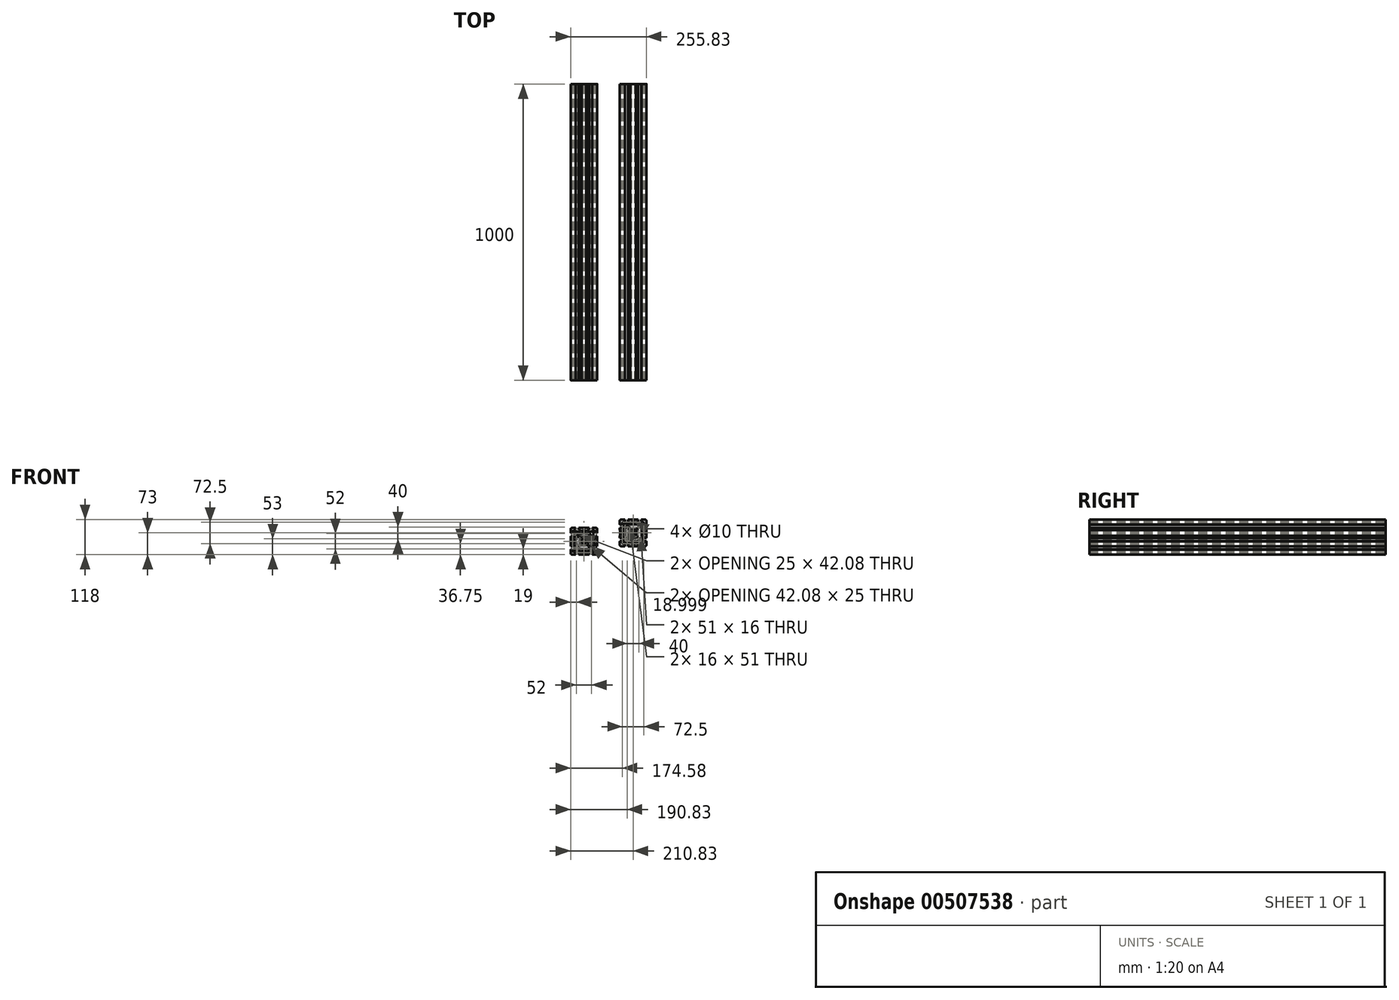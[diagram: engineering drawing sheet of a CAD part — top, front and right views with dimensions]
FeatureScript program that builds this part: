
annotation { "Feature Type Name" : "Feature", "Feature Type Description" : "" }
export const myFeature = defineFeature(function(context is Context, id is Id, definition is map)
    precondition{}
    {
        {
            var Q0;
            Q0=qCreatedBy(makeId("Front.planeOp"),FACE);
            var sketch = newSketch(context, id + "F0", { "sketchPlane" : qUnion([Q0])});
            skLineSegment(sketch, "E0", {"start": v(28, 45) * mm, "end": v(28, 44.5) * mm});
            skLineSegment(sketch, "E1", {"start": v(28, 44.5) * mm, "end": v(27.5, 44.5) * mm});
            skLineSegment(sketch, "E2", {"start": v(27.5, 44.5) * mm, "end": v(27.5, 39) * mm});
            skLineSegment(sketch, "E3", {"start": v(27.5, 39) * mm, "end": v(33.5, 39) * mm});
            skLineSegment(sketch, "E4", {"start": v(33.5, 39) * mm, "end": v(33.5, 36) * mm});
            skLineSegment(sketch, "E5", {"start": v(33.5, 36) * mm, "end": v(29.5, 32) * mm});
            skLineSegment(sketch, "E6", {"start": v(29.5, 32) * mm, "end": v(12.5, 32) * mm});
            skLineSegment(sketch, "E7", {"start": v(12.5, 32) * mm, "end": v(12.5, 39) * mm});
            skLineSegment(sketch, "E8", {"start": v(12.5, 39) * mm, "end": v(17.5, 39) * mm});
            skLineSegment(sketch, "E9", {"start": v(17.5, 39) * mm, "end": v(17.5, 44.5) * mm});
            skLineSegment(sketch, "E10", {"start": v(17.5, 44.5) * mm, "end": v(17, 44.5) * mm});
            skLineSegment(sketch, "E11", {"start": v(17, 44.5) * mm, "end": v(17, 45) * mm});
            skLineSegment(sketch, "E12", {"start": v(45, 28) * mm, "end": v(44.5, 28) * mm});
            skLineSegment(sketch, "E13", {"start": v(44.5, 28) * mm, "end": v(44.5, 27.5) * mm});
            skLineSegment(sketch, "E14", {"start": v(44.5, 27.5) * mm, "end": v(39, 27.5) * mm});
            skLineSegment(sketch, "E15", {"start": v(39, 27.5) * mm, "end": v(39, 33.5) * mm});
            skLineSegment(sketch, "E16", {"start": v(39, 33.5) * mm, "end": v(36, 33.5) * mm});
            skLineSegment(sketch, "E17", {"start": v(36, 33.5) * mm, "end": v(32, 29.5) * mm});
            skLineSegment(sketch, "E18", {"start": v(32, 29.5) * mm, "end": v(32, 12.5) * mm});
            skLineSegment(sketch, "E19", {"start": v(32, 12.5) * mm, "end": v(39, 12.5) * mm});
            skLineSegment(sketch, "E20", {"start": v(39, 12.5) * mm, "end": v(39, 17.5) * mm});
            skLineSegment(sketch, "E21", {"start": v(39, 17.5) * mm, "end": v(44.5, 17.5) * mm});
            skLineSegment(sketch, "E22", {"start": v(44.5, 17.5) * mm, "end": v(44.5, 17) * mm});
            skLineSegment(sketch, "E23", {"start": v(44.5, 17) * mm, "end": v(45, 17) * mm});
            skLineSegment(sketch, "E24", {"start": v(45, 28) * mm, "end": v(45, 40) * mm});
            skLineSegment(sketch, "E25", {"start": v(28, 45) * mm, "end": v(40, 45) * mm});
            skPoint(sketch, "E26.visualSharp", {"position": v(45, 45) * mm});
            skArc(sketch, "E26.filletArc", {"start": v(45, 40) * mm, "mid": v(43.54, 43.54) * mm, "end": v(40, 45) * mm});
            skLineSegment(sketch, "E27", {"start": v(17, 45) * mm, "end": v(9.5, 45) * mm});
            skLineSegment(sketch, "E28", {"start": v(9.5, 45) * mm, "end": v(9.5, 44.5) * mm});
            skLineSegment(sketch, "E29", {"start": v(9.5, 44.5) * mm, "end": v(0, 44.5) * mm});
            skLineSegment(sketch, "E30", {"start": v(0, 44.5) * mm, "end": v(0, 41.25) * mm});
            skLineSegment(sketch, "E31", {"start": v(45, 17) * mm, "end": v(45, 9.5) * mm});
            skLineSegment(sketch, "E32", {"start": v(45, 9.5) * mm, "end": v(44.5, 9.5) * mm});
            skLineSegment(sketch, "E33", {"start": v(44.5, 9.5) * mm, "end": v(44.5, 0) * mm});
            skLineSegment(sketch, "E34", {"start": v(44.5, 0) * mm, "end": v(41.25, 0) * mm});
            skLineSegment(sketch, "E35.bottom", {"start": v(7.5, 0) * mm, "end": v(12, 0) * mm});
            skLineSegment(sketch, "E35.top", {"start": v(0, 28) * mm, "end": v(25.5, 28) * mm});
            skLineSegment(sketch, "E35.right", {"start": v(28, 0) * mm, "end": v(28, 25.5) * mm});
            skLineSegment(sketch, "E36.top", {"start": v(0, 12) * mm, "end": v(9.5, 12) * mm});
            skLineSegment(sketch, "E36.left", {"start": v(0, 7.5) * mm, "end": v(0, 12) * mm});
            skLineSegment(sketch, "E36.right", {"start": v(12, 0) * mm, "end": v(12, 9.5) * mm});
            skArc(sketch, "E37", {"start": v(7.5, 0) * mm, "mid": v(5.3, 5.3) * mm, "end": v(0, 7.5) * mm});
            skLineSegment(sketch, "E38", {"start": v(25.5, 28) * mm, "end": v(9.5, 12) * mm});
            skLineSegment(sketch, "E39", {"start": v(28, 25.5) * mm, "end": v(12, 9.5) * mm});
            skLineSegment(sketch, "E40.trimOffspring", {"start": v(12, 0) * mm, "end": v(7.5, 0) * mm});
            skLineSegment(sketch, "E41.trimOffspring", {"start": v(0, 12) * mm, "end": v(0, 7.5) * mm});
            skArc(sketch, "E42", {"start": v(41.25, 0) * mm, "mid": v(36.25, 5) * mm, "end": v(31.25, 0) * mm});
            skArc(sketch, "E43", {"start": v(0, 31.25) * mm, "mid": v(5, 36.25) * mm, "end": v(0, 41.25) * mm});
            skLineSegment(sketch, "E44.trimOffspring", {"start": v(0, 31.25) * mm, "end": v(0, 28) * mm});
            skLineSegment(sketch, "E45.trimOffspring", {"start": v(31.25, 0) * mm, "end": v(28, 0) * mm});
            skLineSegment(sketch, "E46.1.0", {"start": v(-28, 0) * mm, "end": v(-28, 25.5) * mm});
            skLineSegment(sketch, "E46.1.1", {"start": v(0, 28) * mm, "end": v(-25.5, 28) * mm});
            skPoint(sketch, "E46.1.2", {"position": v(-45, 45) * mm});
            skArc(sketch, "E46.1.3", {"start": v(0, 41.25) * mm, "mid": v(-5, 36.25) * mm, "end": v(0, 31.25) * mm});
            skLineSegment(sketch, "E46.1.4", {"start": v(-25.5, 28) * mm, "end": v(-9.5, 12) * mm});
            skLineSegment(sketch, "E46.1.5", {"start": v(-44.5, 9.5) * mm, "end": v(-44.5, 0) * mm});
            skLineSegment(sketch, "E46.1.6", {"start": v(-28, 25.5) * mm, "end": v(-12, 9.5) * mm});
            skLineSegment(sketch, "E46.1.7", {"start": v(-28, 45) * mm, "end": v(-40, 45) * mm});
            skLineSegment(sketch, "E46.1.8", {"start": v(-32, 29.5) * mm, "end": v(-32, 12.5) * mm});
            skArc(sketch, "E46.1.9", {"start": v(-31.25, 0) * mm, "mid": v(-36.25, 5) * mm, "end": v(-41.25, 0) * mm});
            skLineSegment(sketch, "E46.1.10", {"start": v(-9.5, 44.5) * mm, "end": v(0, 44.5) * mm});
            skLineSegment(sketch, "E46.1.11", {"start": v(-12.5, 32) * mm, "end": v(-12.5, 39) * mm});
            skLineSegment(sketch, "E46.1.12", {"start": v(-12, 0) * mm, "end": v(-12, 9.5) * mm});
            skLineSegment(sketch, "E46.1.13", {"start": v(-45, 17) * mm, "end": v(-45, 9.5) * mm});
            skArc(sketch, "E46.1.14", {"start": v(-40, 45) * mm, "mid": v(-43.54, 43.54) * mm, "end": v(-45, 40) * mm});
            skArc(sketch, "E46.1.15", {"start": v(0, 7.5) * mm, "mid": v(-5.3, 5.3) * mm, "end": v(-7.5, 0) * mm});
            skLineSegment(sketch, "E46.1.16", {"start": v(-45, 28) * mm, "end": v(-45, 40) * mm});
            skLineSegment(sketch, "E46.1.17", {"start": v(0, 12) * mm, "end": v(-9.5, 12) * mm});
            skLineSegment(sketch, "E46.1.18", {"start": v(-17, 45) * mm, "end": v(-9.5, 45) * mm});
            skLineSegment(sketch, "E46.1.19", {"start": v(-32, 12.5) * mm, "end": v(-39, 12.5) * mm});
            skLineSegment(sketch, "E46.1.20", {"start": v(-29.5, 32) * mm, "end": v(-12.5, 32) * mm});
            skLineSegment(sketch, "E46.1.21", {"start": v(-12.5, 39) * mm, "end": v(-17.5, 39) * mm});
            skLineSegment(sketch, "E46.1.22", {"start": v(-17.5, 39) * mm, "end": v(-17.5, 44.5) * mm});
            skLineSegment(sketch, "E46.1.23", {"start": v(-44.5, 0) * mm, "end": v(-41.25, 0) * mm});
            skLineSegment(sketch, "E46.1.24", {"start": v(-27.5, 39) * mm, "end": v(-33.5, 39) * mm});
            skLineSegment(sketch, "E46.1.25", {"start": v(-36, 33.5) * mm, "end": v(-32, 29.5) * mm});
            skLineSegment(sketch, "E46.1.26", {"start": v(-39, 12.5) * mm, "end": v(-39, 17.5) * mm});
            skLineSegment(sketch, "E46.1.27", {"start": v(-39, 17.5) * mm, "end": v(-44.5, 17.5) * mm});
            skLineSegment(sketch, "E46.1.28", {"start": v(-33.5, 39) * mm, "end": v(-33.5, 36) * mm});
            skLineSegment(sketch, "E46.1.29", {"start": v(-33.5, 36) * mm, "end": v(-29.5, 32) * mm});
            skLineSegment(sketch, "E46.1.30", {"start": v(-31.25, 0) * mm, "end": v(-28, 0) * mm});
            skLineSegment(sketch, "E46.1.33", {"start": v(-12, 0) * mm, "end": v(-7.5, 0) * mm});
            skLineSegment(sketch, "E46.1.34", {"start": v(-27.5, 44.5) * mm, "end": v(-27.5, 39) * mm});
            skLineSegment(sketch, "E46.1.35", {"start": v(-44.5, 27.5) * mm, "end": v(-39, 27.5) * mm});
            skLineSegment(sketch, "E46.1.36", {"start": v(-39, 27.5) * mm, "end": v(-39, 33.5) * mm});
            skLineSegment(sketch, "E46.1.37", {"start": v(-39, 33.5) * mm, "end": v(-36, 33.5) * mm});
            skLineSegment(sketch, "E46.1.39", {"start": v(-7.5, 0) * mm, "end": v(-12, 0) * mm});
            skLineSegment(sketch, "E46.1.40", {"start": v(-45, 28) * mm, "end": v(-44.5, 28) * mm});
            skLineSegment(sketch, "E46.1.41", {"start": v(-44.5, 28) * mm, "end": v(-44.5, 27.5) * mm});
            skLineSegment(sketch, "E46.1.42", {"start": v(-9.5, 45) * mm, "end": v(-9.5, 44.5) * mm});
            skLineSegment(sketch, "E46.1.43", {"start": v(-17.5, 44.5) * mm, "end": v(-17, 44.5) * mm});
            skLineSegment(sketch, "E46.1.45", {"start": v(-17, 44.5) * mm, "end": v(-17, 45) * mm});
            skLineSegment(sketch, "E46.1.46", {"start": v(-45, 9.5) * mm, "end": v(-44.5, 9.5) * mm});
            skLineSegment(sketch, "E46.1.47", {"start": v(-44.5, 17) * mm, "end": v(-45, 17) * mm});
            skLineSegment(sketch, "E46.1.49", {"start": v(-44.5, 17.5) * mm, "end": v(-44.5, 17) * mm});
            skLineSegment(sketch, "E46.1.50", {"start": v(-28, 44.5) * mm, "end": v(-27.5, 44.5) * mm});
            skLineSegment(sketch, "E46.1.51", {"start": v(-28, 45) * mm, "end": v(-28, 44.5) * mm});
            skLineSegment(sketch, "E46.2.0", {"start": v(0, -28) * mm, "end": v(-25.5, -28) * mm});
            skLineSegment(sketch, "E46.2.1", {"start": v(-28, 0) * mm, "end": v(-28, -25.5) * mm});
            skPoint(sketch, "E46.2.2", {"position": v(-45, -45) * mm});
            skArc(sketch, "E46.2.3", {"start": v(-41.25, 0) * mm, "mid": v(-36.25, -5) * mm, "end": v(-31.25, 0) * mm});
            skLineSegment(sketch, "E46.2.4", {"start": v(-28, -25.5) * mm, "end": v(-12, -9.5) * mm});
            skLineSegment(sketch, "E46.2.5", {"start": v(-9.5, -44.5) * mm, "end": v(0, -44.5) * mm});
            skLineSegment(sketch, "E46.2.6", {"start": v(-25.5, -28) * mm, "end": v(-9.5, -12) * mm});
            skLineSegment(sketch, "E46.2.7", {"start": v(-45, -28) * mm, "end": v(-45, -40) * mm});
            skLineSegment(sketch, "E46.2.8", {"start": v(-29.5, -32) * mm, "end": v(-12.5, -32) * mm});
            skArc(sketch, "E46.2.9", {"start": v(0, -31.25) * mm, "mid": v(-5, -36.25) * mm, "end": v(0, -41.25) * mm});
            skLineSegment(sketch, "E46.2.10", {"start": v(-44.5, -9.5) * mm, "end": v(-44.5, 0) * mm});
            skLineSegment(sketch, "E46.2.11", {"start": v(-32, -12.5) * mm, "end": v(-39, -12.5) * mm});
            skLineSegment(sketch, "E46.2.12", {"start": v(0, -12) * mm, "end": v(-9.5, -12) * mm});
            skLineSegment(sketch, "E46.2.13", {"start": v(-17, -45) * mm, "end": v(-9.5, -45) * mm});
            skArc(sketch, "E46.2.14", {"start": v(-45, -40) * mm, "mid": v(-43.54, -43.54) * mm, "end": v(-40, -45) * mm});
            skArc(sketch, "E46.2.15", {"start": v(-7.5, 0) * mm, "mid": v(-5.3, -5.3) * mm, "end": v(0, -7.5) * mm});
            skLineSegment(sketch, "E46.2.16", {"start": v(-28, -45) * mm, "end": v(-40, -45) * mm});
            skLineSegment(sketch, "E46.2.17", {"start": v(-12, 0) * mm, "end": v(-12, -9.5) * mm});
            skLineSegment(sketch, "E46.2.18", {"start": v(-45, -17) * mm, "end": v(-45, -9.5) * mm});
            skLineSegment(sketch, "E46.2.19", {"start": v(-12.5, -32) * mm, "end": v(-12.5, -39) * mm});
            skLineSegment(sketch, "E46.2.20", {"start": v(-32, -29.5) * mm, "end": v(-32, -12.5) * mm});
            skLineSegment(sketch, "E46.2.21", {"start": v(-39, -12.5) * mm, "end": v(-39, -17.5) * mm});
            skLineSegment(sketch, "E46.2.22", {"start": v(-39, -17.5) * mm, "end": v(-44.5, -17.5) * mm});
            skLineSegment(sketch, "E46.2.23", {"start": v(0, -44.5) * mm, "end": v(0, -41.25) * mm});
            skLineSegment(sketch, "E46.2.24", {"start": v(-39, -27.5) * mm, "end": v(-39, -33.5) * mm});
            skLineSegment(sketch, "E46.2.25", {"start": v(-33.5, -36) * mm, "end": v(-29.5, -32) * mm});
            skLineSegment(sketch, "E46.2.26", {"start": v(-12.5, -39) * mm, "end": v(-17.5, -39) * mm});
            skLineSegment(sketch, "E46.2.27", {"start": v(-17.5, -39) * mm, "end": v(-17.5, -44.5) * mm});
            skLineSegment(sketch, "E46.2.28", {"start": v(-39, -33.5) * mm, "end": v(-36, -33.5) * mm});
            skLineSegment(sketch, "E46.2.29", {"start": v(-36, -33.5) * mm, "end": v(-32, -29.5) * mm});
            skLineSegment(sketch, "E46.2.30", {"start": v(0, -31.25) * mm, "end": v(0, -28) * mm});
            skLineSegment(sketch, "E46.2.31", {"start": v(-31.25, 0) * mm, "end": v(-28, 0) * mm});
            skLineSegment(sketch, "E46.2.32", {"start": v(-44.5, 0) * mm, "end": v(-41.25, 0) * mm});
            skLineSegment(sketch, "E46.2.33", {"start": v(0, -12) * mm, "end": v(0, -7.5) * mm});
            skLineSegment(sketch, "E46.2.34", {"start": v(-44.5, -27.5) * mm, "end": v(-39, -27.5) * mm});
            skLineSegment(sketch, "E46.2.35", {"start": v(-27.5, -44.5) * mm, "end": v(-27.5, -39) * mm});
            skLineSegment(sketch, "E46.2.36", {"start": v(-27.5, -39) * mm, "end": v(-33.5, -39) * mm});
            skLineSegment(sketch, "E46.2.37", {"start": v(-33.5, -39) * mm, "end": v(-33.5, -36) * mm});
            skLineSegment(sketch, "E46.2.38", {"start": v(-12, 0) * mm, "end": v(-7.5, 0) * mm});
            skLineSegment(sketch, "E46.2.39", {"start": v(0, -7.5) * mm, "end": v(0, -12) * mm});
            skLineSegment(sketch, "E46.2.40", {"start": v(-28, -45) * mm, "end": v(-28, -44.5) * mm});
            skLineSegment(sketch, "E46.2.41", {"start": v(-28, -44.5) * mm, "end": v(-27.5, -44.5) * mm});
            skLineSegment(sketch, "E46.2.42", {"start": v(-45, -9.5) * mm, "end": v(-44.5, -9.5) * mm});
            skLineSegment(sketch, "E46.2.43", {"start": v(-44.5, -17.5) * mm, "end": v(-44.5, -17) * mm});
            skLineSegment(sketch, "E46.2.44", {"start": v(-7.5, 0) * mm, "end": v(-12, 0) * mm});
            skLineSegment(sketch, "E46.2.45", {"start": v(-44.5, -17) * mm, "end": v(-45, -17) * mm});
            skLineSegment(sketch, "E46.2.46", {"start": v(-9.5, -45) * mm, "end": v(-9.5, -44.5) * mm});
            skLineSegment(sketch, "E46.2.47", {"start": v(-17, -44.5) * mm, "end": v(-17, -45) * mm});
            skLineSegment(sketch, "E46.2.48", {"start": v(-7.5, 0) * mm, "end": v(-12, 0) * mm});
            skLineSegment(sketch, "E46.2.49", {"start": v(-17.5, -44.5) * mm, "end": v(-17, -44.5) * mm});
            skLineSegment(sketch, "E46.2.50", {"start": v(-44.5, -28) * mm, "end": v(-44.5, -27.5) * mm});
            skLineSegment(sketch, "E46.2.51", {"start": v(-45, -28) * mm, "end": v(-44.5, -28) * mm});
            skLineSegment(sketch, "E46.3.0", {"start": v(28, 0) * mm, "end": v(28, -25.5) * mm});
            skLineSegment(sketch, "E46.3.1", {"start": v(0, -28) * mm, "end": v(25.5, -28) * mm});
            skPoint(sketch, "E46.3.2", {"position": v(45, -45) * mm});
            skArc(sketch, "E46.3.3", {"start": v(0, -41.25) * mm, "mid": v(5, -36.25) * mm, "end": v(0, -31.25) * mm});
            skLineSegment(sketch, "E46.3.4", {"start": v(25.5, -28) * mm, "end": v(9.5, -12) * mm});
            skLineSegment(sketch, "E46.3.5", {"start": v(44.5, -9.5) * mm, "end": v(44.5, 0) * mm});
            skLineSegment(sketch, "E46.3.6", {"start": v(28, -25.5) * mm, "end": v(12, -9.5) * mm});
            skLineSegment(sketch, "E46.3.7", {"start": v(28, -45) * mm, "end": v(40, -45) * mm});
            skLineSegment(sketch, "E46.3.8", {"start": v(32, -29.5) * mm, "end": v(32, -12.5) * mm});
            skArc(sketch, "E46.3.9", {"start": v(31.25, 0) * mm, "mid": v(36.25, -5) * mm, "end": v(41.25, 0) * mm});
            skLineSegment(sketch, "E46.3.10", {"start": v(9.5, -44.5) * mm, "end": v(0, -44.5) * mm});
            skLineSegment(sketch, "E46.3.11", {"start": v(12.5, -32) * mm, "end": v(12.5, -39) * mm});
            skLineSegment(sketch, "E46.3.12", {"start": v(12, 0) * mm, "end": v(12, -9.5) * mm});
            skLineSegment(sketch, "E46.3.13", {"start": v(45, -17) * mm, "end": v(45, -9.5) * mm});
            skArc(sketch, "E46.3.14", {"start": v(40, -45) * mm, "mid": v(43.54, -43.54) * mm, "end": v(45, -40) * mm});
            skArc(sketch, "E46.3.15", {"start": v(0, -7.5) * mm, "mid": v(5.3, -5.3) * mm, "end": v(7.5, 0) * mm});
            skLineSegment(sketch, "E46.3.16", {"start": v(45, -28) * mm, "end": v(45, -40) * mm});
            skLineSegment(sketch, "E46.3.17", {"start": v(0, -12) * mm, "end": v(9.5, -12) * mm});
            skLineSegment(sketch, "E46.3.18", {"start": v(17, -45) * mm, "end": v(9.5, -45) * mm});
            skLineSegment(sketch, "E46.3.19", {"start": v(32, -12.5) * mm, "end": v(39, -12.5) * mm});
            skLineSegment(sketch, "E46.3.20", {"start": v(29.5, -32) * mm, "end": v(12.5, -32) * mm});
            skLineSegment(sketch, "E46.3.21", {"start": v(12.5, -39) * mm, "end": v(17.5, -39) * mm});
            skLineSegment(sketch, "E46.3.22", {"start": v(17.5, -39) * mm, "end": v(17.5, -44.5) * mm});
            skLineSegment(sketch, "E46.3.24", {"start": v(27.5, -39) * mm, "end": v(33.5, -39) * mm});
            skLineSegment(sketch, "E46.3.25", {"start": v(36, -33.5) * mm, "end": v(32, -29.5) * mm});
            skLineSegment(sketch, "E46.3.26", {"start": v(39, -12.5) * mm, "end": v(39, -17.5) * mm});
            skLineSegment(sketch, "E46.3.27", {"start": v(39, -17.5) * mm, "end": v(44.5, -17.5) * mm});
            skLineSegment(sketch, "E46.3.28", {"start": v(33.5, -39) * mm, "end": v(33.5, -36) * mm});
            skLineSegment(sketch, "E46.3.29", {"start": v(33.5, -36) * mm, "end": v(29.5, -32) * mm});
            skLineSegment(sketch, "E46.3.31", {"start": v(0, -31.25) * mm, "end": v(0, -28) * mm});
            skLineSegment(sketch, "E46.3.32", {"start": v(0, -44.5) * mm, "end": v(0, -41.25) * mm});
            skLineSegment(sketch, "E46.3.34", {"start": v(27.5, -44.5) * mm, "end": v(27.5, -39) * mm});
            skLineSegment(sketch, "E46.3.35", {"start": v(44.5, -27.5) * mm, "end": v(39, -27.5) * mm});
            skLineSegment(sketch, "E46.3.36", {"start": v(39, -27.5) * mm, "end": v(39, -33.5) * mm});
            skLineSegment(sketch, "E46.3.37", {"start": v(39, -33.5) * mm, "end": v(36, -33.5) * mm});
            skLineSegment(sketch, "E46.3.38", {"start": v(0, -12) * mm, "end": v(0, -7.5) * mm});
            skLineSegment(sketch, "E46.3.40", {"start": v(45, -28) * mm, "end": v(44.5, -28) * mm});
            skLineSegment(sketch, "E46.3.41", {"start": v(44.5, -28) * mm, "end": v(44.5, -27.5) * mm});
            skLineSegment(sketch, "E46.3.42", {"start": v(9.5, -45) * mm, "end": v(9.5, -44.5) * mm});
            skLineSegment(sketch, "E46.3.43", {"start": v(17.5, -44.5) * mm, "end": v(17, -44.5) * mm});
            skLineSegment(sketch, "E46.3.44", {"start": v(0, -7.5) * mm, "end": v(0, -12) * mm});
            skLineSegment(sketch, "E46.3.45", {"start": v(17, -44.5) * mm, "end": v(17, -45) * mm});
            skLineSegment(sketch, "E46.3.46", {"start": v(45, -9.5) * mm, "end": v(44.5, -9.5) * mm});
            skLineSegment(sketch, "E46.3.47", {"start": v(44.5, -17) * mm, "end": v(45, -17) * mm});
            skLineSegment(sketch, "E46.3.48", {"start": v(0, -7.5) * mm, "end": v(0, -12) * mm});
            skLineSegment(sketch, "E46.3.49", {"start": v(44.5, -17.5) * mm, "end": v(44.5, -17) * mm});
            skLineSegment(sketch, "E46.3.50", {"start": v(28, -44.5) * mm, "end": v(27.5, -44.5) * mm});
            skLineSegment(sketch, "E46.3.51", {"start": v(28, -45) * mm, "end": v(28, -44.5) * mm});
            skPoint(sketch, "E46.center", {"position": v(0, 0) * mm});
            skLineSegment(sketch, "E47", {"start": v(-165.83, 16.5) * mm, "end": v(-157.83, 16.5) * mm});
            skLineSegment(sketch, "E48", {"start": v(-157.83, 16.5) * mm, "end": v(-157.83, 17) * mm});
            skLineSegment(sketch, "E49", {"start": v(-157.83, 17) * mm, "end": v(-148.83, 17) * mm});
            skLineSegment(sketch, "E50", {"start": v(-148.83, 17) * mm, "end": v(-148.83, 16.5) * mm});
            skLineSegment(sketch, "E51", {"start": v(-148.83, 16.5) * mm, "end": v(-148.33, 16.5) * mm});
            skLineSegment(sketch, "E52", {"start": v(-148.33, 16.5) * mm, "end": v(-148.33, 11) * mm});
            skLineSegment(sketch, "E53", {"start": v(-148.33, 11) * mm, "end": v(-154.83, 11) * mm});
            skLineSegment(sketch, "E54", {"start": v(-154.83, 11) * mm, "end": v(-154.83, 4) * mm});
            skLineSegment(sketch, "E55", {"start": v(-154.83, 4) * mm, "end": v(-135.95, 4) * mm});
            skLineSegment(sketch, "E56", {"start": v(-135.95, 4) * mm, "end": v(-131.83, 8.12) * mm});
            skLineSegment(sketch, "E57", {"start": v(-131.83, 8.12) * mm, "end": v(-131.83, 11) * mm});
            skLineSegment(sketch, "E58", {"start": v(-131.83, 11) * mm, "end": v(-138.33, 11) * mm});
            skLineSegment(sketch, "E59", {"start": v(-138.33, 11) * mm, "end": v(-138.33, 16.5) * mm});
            skLineSegment(sketch, "E60", {"start": v(-138.33, 16.5) * mm, "end": v(-137.83, 16.5) * mm});
            skLineSegment(sketch, "E61", {"start": v(-137.83, 16.5) * mm, "end": v(-137.83, 17) * mm});
            skLineSegment(sketch, "E62", {"start": v(-137.83, 17) * mm, "end": v(-125.83, 17) * mm});
            skArc(sketch, "E63", {"start": v(-125.83, 17) * mm, "mid": v(-123.92, 16.62) * mm, "end": v(-122.3, 15.54) * mm});
            skLineSegment(sketch, "E64", {"start": v(-165.83, 10.5) * mm, "end": v(-163.87, 10.5) * mm});
            skLineSegment(sketch, "E65", {"start": v(-163.87, 10.5) * mm, "end": v(-163.87, 9.5) * mm});
            skArc(sketch, "E66", {"start": v(-163.87, 9.5) * mm, "mid": v(-160.93, 5.88) * mm, "end": v(-162.26, 1.4) * mm});
            skArc(sketch, "E67", {"start": v(-162.26, 1.4) * mm, "mid": v(-162.67, -0.77) * mm, "end": v(-160.83, -2) * mm});
            skLineSegment(sketch, "E68", {"start": v(-160.83, -2) * mm, "end": v(-146.78, -2) * mm});
            skArc(sketch, "E69", {"start": v(-146.78, -2) * mm, "mid": v(-144.93, -3.23) * mm, "end": v(-145.37, -5.41) * mm});
            skLineSegment(sketch, "E70", {"start": v(-145.37, -5.41) * mm, "end": v(-154.45, -14.5) * mm});
            skLineSegment(sketch, "E71", {"start": v(-154.45, -14.5) * mm, "end": v(-165.83, -14.5) * mm});
            skArc(sketch, "E72", {"start": v(-165.83, -20.5) * mm, "mid": v(-162.96, -21.07) * mm, "end": v(-160.53, -22.7) * mm});
            skLineSegment(sketch, "E73", {"start": v(-160.53, -22.7) * mm, "end": v(-165.83, -28) * mm, "construction": true});
            skLineSegment(sketch, "E74", {"start": v(-165.83, -20.5) * mm, "end": v(-165.83, -28) * mm, "construction": true});
            skLineSegment(sketch, "E75.MirrorCS", {"start": v(-121.33, -0.5) * mm, "end": v(-121.33, 0) * mm});
            skLineSegment(sketch, "E76.MirrorCS", {"start": v(-129.7, 6) * mm, "end": v(-126.83, 6) * mm});
            skLineSegment(sketch, "E77.MirrorCS", {"start": v(-121.33, -11) * mm, "end": v(-121.33, -10.5) * mm});
            skLineSegment(sketch, "E78.MirrorCS", {"start": v(-120.83, -11) * mm, "end": v(-121.33, -11) * mm});
            skLineSegment(sketch, "E79.MirrorCS", {"start": v(-127.33, -26.04) * mm, "end": v(-128.33, -26.04) * mm});
            skLineSegment(sketch, "E80.MirrorCS", {"start": v(-121.33, -20) * mm, "end": v(-120.83, -20) * mm});
            skLineSegment(sketch, "E81.MirrorCS", {"start": v(-121.33, 0) * mm, "end": v(-120.83, 0) * mm});
            skArc(sketch, "E82.MirrorCS", {"start": v(-136.43, -24.43) * mm, "mid": v(-138.6, -24.84) * mm, "end": v(-139.83, -23) * mm});
            skLineSegment(sketch, "E83.MirrorCS", {"start": v(-127.33, -28) * mm, "end": v(-127.33, -26.04) * mm});
            skArc(sketch, "E84.MirrorCS", {"start": v(-120.83, 12) * mm, "mid": v(-121.21, 13.91) * mm, "end": v(-122.3, 15.54) * mm});
            skLineSegment(sketch, "E85.MirrorCS", {"start": v(-126.83, -0.5) * mm, "end": v(-121.33, -0.5) * mm});
            skArc(sketch, "E86.MirrorCS", {"start": v(-158.33, -28) * mm, "mid": v(-158.9, -25.13) * mm, "end": v(-160.53, -22.7) * mm});
            skLineSegment(sketch, "E87.MirrorCS", {"start": v(-133.83, 1.88) * mm, "end": v(-129.7, 6) * mm});
            skLineSegment(sketch, "E88.MirrorCS", {"start": v(-152.33, -16.62) * mm, "end": v(-152.33, -28) * mm});
            skLineSegment(sketch, "E89.MirrorCS", {"start": v(-133.83, -17) * mm, "end": v(-133.83, 1.88) * mm});
            skLineSegment(sketch, "E90.MirrorCS", {"start": v(-143.25, -7.54) * mm, "end": v(-152.33, -16.62) * mm});
            skLineSegment(sketch, "E91.MirrorCS", {"start": v(-126.83, -17) * mm, "end": v(-133.83, -17) * mm});
            skLineSegment(sketch, "E92.MirrorCS", {"start": v(-126.83, -10.5) * mm, "end": v(-126.83, -17) * mm});
            skArc(sketch, "E93.MirrorCS", {"start": v(-139.83, -8.95) * mm, "mid": v(-141.07, -7.1) * mm, "end": v(-143.25, -7.54) * mm});
            skLineSegment(sketch, "E94.MirrorCS", {"start": v(-121.33, -10.5) * mm, "end": v(-126.83, -10.5) * mm});
            skLineSegment(sketch, "E95.MirrorCS", {"start": v(-139.83, -23) * mm, "end": v(-139.83, -8.95) * mm});
            skArc(sketch, "E96.MirrorCS", {"start": v(-128.33, -26.04) * mm, "mid": v(-131.95, -23.1) * mm, "end": v(-136.43, -24.43) * mm});
            skLineSegment(sketch, "E97.MirrorCS", {"start": v(-120.83, -20) * mm, "end": v(-120.83, -11) * mm});
            skLineSegment(sketch, "E98.MirrorCS", {"start": v(-121.33, -28) * mm, "end": v(-121.33, -20) * mm});
            skLineSegment(sketch, "E99.MirrorCS", {"start": v(-120.83, 0) * mm, "end": v(-120.83, 12) * mm});
            skLineSegment(sketch, "E100.MirrorCS", {"start": v(-126.83, 6) * mm, "end": v(-126.83, -0.5) * mm});
            skLineSegment(sketch, "E101.MirrorCS", {"start": v(-158.33, -28) * mm, "end": v(-165.83, -28) * mm, "construction": true});
            skArc(sketch, "E102.1.0", {"start": v(-158.33, -28) * mm, "mid": v(-158.9, -30.87) * mm, "end": v(-160.53, -33.3) * mm});
            skLineSegment(sketch, "E102.1.1", {"start": v(-133.83, -57.88) * mm, "end": v(-129.7, -62) * mm});
            skArc(sketch, "E102.1.2", {"start": v(-128.33, -29.96) * mm, "mid": v(-131.95, -32.9) * mm, "end": v(-136.43, -31.57) * mm});
            skLineSegment(sketch, "E102.1.3", {"start": v(-165.83, -72.5) * mm, "end": v(-157.83, -72.5) * mm});
            skLineSegment(sketch, "E102.1.4", {"start": v(-120.83, -36) * mm, "end": v(-120.83, -45) * mm});
            skLineSegment(sketch, "E102.1.5", {"start": v(-121.33, -28) * mm, "end": v(-121.33, -36) * mm});
            skLineSegment(sketch, "E102.1.6", {"start": v(-148.33, -72.5) * mm, "end": v(-148.33, -67) * mm});
            skLineSegment(sketch, "E102.1.8", {"start": v(-154.45, -41.5) * mm, "end": v(-165.83, -41.5) * mm});
            skLineSegment(sketch, "E102.1.9", {"start": v(-154.83, -67) * mm, "end": v(-154.83, -60) * mm});
            skLineSegment(sketch, "E102.1.10", {"start": v(-126.83, -55.5) * mm, "end": v(-121.33, -55.5) * mm});
            skLineSegment(sketch, "E102.1.11", {"start": v(-148.33, -67) * mm, "end": v(-154.83, -67) * mm});
            skLineSegment(sketch, "E102.1.12", {"start": v(-154.83, -60) * mm, "end": v(-135.95, -60) * mm});
            skLineSegment(sketch, "E102.1.13", {"start": v(-160.53, -33.3) * mm, "end": v(-165.83, -28) * mm, "construction": true});
            skLineSegment(sketch, "E102.1.14", {"start": v(-145.37, -50.59) * mm, "end": v(-154.45, -41.5) * mm});
            skLineSegment(sketch, "E102.1.15", {"start": v(-126.83, -62) * mm, "end": v(-126.83, -55.5) * mm});
            skLineSegment(sketch, "E102.1.16", {"start": v(-152.33, -39.38) * mm, "end": v(-152.33, -28) * mm});
            skLineSegment(sketch, "E102.1.17", {"start": v(-135.95, -60) * mm, "end": v(-131.83, -64.12) * mm});
            skLineSegment(sketch, "E102.1.18", {"start": v(-133.83, -39) * mm, "end": v(-133.83, -57.88) * mm});
            skLineSegment(sketch, "E102.1.19", {"start": v(-143.25, -48.46) * mm, "end": v(-152.33, -39.38) * mm});
            skLineSegment(sketch, "E102.1.20", {"start": v(-126.83, -39) * mm, "end": v(-133.83, -39) * mm});
            skLineSegment(sketch, "E102.1.21", {"start": v(-139.83, -33) * mm, "end": v(-139.83, -47.05) * mm});
            skLineSegment(sketch, "E102.1.22", {"start": v(-121.33, -45.5) * mm, "end": v(-126.83, -45.5) * mm});
            skLineSegment(sketch, "E102.1.23", {"start": v(-137.83, -73) * mm, "end": v(-125.83, -73) * mm});
            skLineSegment(sketch, "E102.1.24", {"start": v(-160.83, -54) * mm, "end": v(-146.78, -54) * mm});
            skLineSegment(sketch, "E102.1.25", {"start": v(-157.83, -73) * mm, "end": v(-148.83, -73) * mm});
            skLineSegment(sketch, "E102.1.26", {"start": v(-120.83, -56) * mm, "end": v(-120.83, -68) * mm});
            skArc(sketch, "E102.1.27", {"start": v(-163.87, -65.5) * mm, "mid": v(-160.93, -61.88) * mm, "end": v(-162.26, -57.4) * mm});
            skLineSegment(sketch, "E102.1.28", {"start": v(-131.83, -67) * mm, "end": v(-138.33, -67) * mm});
            skLineSegment(sketch, "E102.1.29", {"start": v(-138.33, -67) * mm, "end": v(-138.33, -72.5) * mm});
            skLineSegment(sketch, "E102.1.30", {"start": v(-126.83, -45.5) * mm, "end": v(-126.83, -39) * mm});
            skArc(sketch, "E102.1.31", {"start": v(-165.83, -35.5) * mm, "mid": v(-162.96, -34.93) * mm, "end": v(-160.53, -33.3) * mm});
            skLineSegment(sketch, "E102.1.32", {"start": v(-165.83, -35.5) * mm, "end": v(-165.83, -28) * mm, "construction": true});
            skLineSegment(sketch, "E102.1.33", {"start": v(-121.33, -45) * mm, "end": v(-121.33, -45.5) * mm});
            skArc(sketch, "E102.1.34", {"start": v(-162.26, -57.4) * mm, "mid": v(-162.67, -55.23) * mm, "end": v(-160.83, -54) * mm});
            skArc(sketch, "E102.1.35", {"start": v(-120.83, -68) * mm, "mid": v(-121.21, -69.91) * mm, "end": v(-122.3, -71.54) * mm});
            skLineSegment(sketch, "E102.1.36", {"start": v(-163.87, -66.5) * mm, "end": v(-163.87, -65.5) * mm});
            skArc(sketch, "E102.1.37", {"start": v(-146.78, -54) * mm, "mid": v(-144.93, -52.77) * mm, "end": v(-145.37, -50.59) * mm});
            skLineSegment(sketch, "E102.1.38", {"start": v(-131.83, -64.12) * mm, "end": v(-131.83, -67) * mm});
            skLineSegment(sketch, "E102.1.39", {"start": v(-148.83, -72.5) * mm, "end": v(-148.33, -72.5) * mm});
            skLineSegment(sketch, "E102.1.40", {"start": v(-129.7, -62) * mm, "end": v(-126.83, -62) * mm});
            skLineSegment(sketch, "E102.1.41", {"start": v(-165.83, -66.5) * mm, "end": v(-163.87, -66.5) * mm});
            skArc(sketch, "E102.1.42", {"start": v(-136.43, -31.57) * mm, "mid": v(-138.6, -31.16) * mm, "end": v(-139.83, -33) * mm});
            skArc(sketch, "E102.1.43", {"start": v(-125.83, -73) * mm, "mid": v(-123.92, -72.62) * mm, "end": v(-122.3, -71.54) * mm});
            skLineSegment(sketch, "E102.1.44", {"start": v(-127.33, -29.96) * mm, "end": v(-128.33, -29.96) * mm});
            skLineSegment(sketch, "E102.1.45", {"start": v(-148.83, -73) * mm, "end": v(-148.83, -72.5) * mm});
            skLineSegment(sketch, "E102.1.46", {"start": v(-157.83, -72.5) * mm, "end": v(-157.83, -73) * mm});
            skLineSegment(sketch, "E102.1.47", {"start": v(-127.33, -28) * mm, "end": v(-127.33, -29.96) * mm});
            skArc(sketch, "E102.1.48", {"start": v(-139.83, -47.05) * mm, "mid": v(-141.07, -48.9) * mm, "end": v(-143.25, -48.46) * mm});
            skLineSegment(sketch, "E102.1.49", {"start": v(-120.83, -45) * mm, "end": v(-121.33, -45) * mm});
            skLineSegment(sketch, "E102.1.50", {"start": v(-121.33, -36) * mm, "end": v(-120.83, -36) * mm});
            skLineSegment(sketch, "E102.1.51", {"start": v(-121.33, -55.5) * mm, "end": v(-121.33, -56) * mm});
            skLineSegment(sketch, "E102.1.52", {"start": v(-121.33, -56) * mm, "end": v(-120.83, -56) * mm});
            skLineSegment(sketch, "E102.1.53", {"start": v(-138.33, -72.5) * mm, "end": v(-137.83, -72.5) * mm});
            skLineSegment(sketch, "E102.1.54", {"start": v(-137.83, -72.5) * mm, "end": v(-137.83, -73) * mm});
            skArc(sketch, "E102.2.0", {"start": v(-165.83, -35.5) * mm, "mid": v(-168.7, -34.93) * mm, "end": v(-171.13, -33.3) * mm});
            skLineSegment(sketch, "E102.2.1", {"start": v(-195.7, -60) * mm, "end": v(-199.83, -64.12) * mm});
            skArc(sketch, "E102.2.2", {"start": v(-167.79, -65.5) * mm, "mid": v(-170.73, -61.88) * mm, "end": v(-169.4, -57.4) * mm});
            skLineSegment(sketch, "E102.2.3", {"start": v(-210.33, -28) * mm, "end": v(-210.33, -36) * mm});
            skLineSegment(sketch, "E102.2.4", {"start": v(-173.83, -73) * mm, "end": v(-182.83, -73) * mm});
            skLineSegment(sketch, "E102.2.5", {"start": v(-165.83, -72.5) * mm, "end": v(-173.83, -72.5) * mm});
            skLineSegment(sketch, "E102.2.6", {"start": v(-210.33, -45.5) * mm, "end": v(-204.83, -45.5) * mm});
            skLineSegment(sketch, "E102.2.7", {"start": v(-165.83, -35.5) * mm, "end": v(-165.83, -28) * mm, "construction": true});
            skLineSegment(sketch, "E102.2.8", {"start": v(-179.33, -39.38) * mm, "end": v(-179.33, -28) * mm});
            skLineSegment(sketch, "E102.2.9", {"start": v(-204.83, -39) * mm, "end": v(-197.83, -39) * mm});
            skLineSegment(sketch, "E102.2.10", {"start": v(-193.33, -67) * mm, "end": v(-193.33, -72.5) * mm});
            skLineSegment(sketch, "E102.2.11", {"start": v(-204.83, -45.5) * mm, "end": v(-204.83, -39) * mm});
            skLineSegment(sketch, "E102.2.12", {"start": v(-197.83, -39) * mm, "end": v(-197.83, -57.88) * mm});
            skLineSegment(sketch, "E102.2.13", {"start": v(-171.13, -33.3) * mm, "end": v(-165.83, -28) * mm, "construction": true});
            skLineSegment(sketch, "E102.2.14", {"start": v(-188.42, -48.46) * mm, "end": v(-179.33, -39.38) * mm});
            skLineSegment(sketch, "E102.2.15", {"start": v(-199.83, -67) * mm, "end": v(-193.33, -67) * mm});
            skLineSegment(sketch, "E102.2.16", {"start": v(-177.2, -41.5) * mm, "end": v(-165.83, -41.5) * mm});
            skLineSegment(sketch, "E102.2.17", {"start": v(-197.83, -57.88) * mm, "end": v(-201.95, -62) * mm});
            skLineSegment(sketch, "E102.2.18", {"start": v(-176.83, -60) * mm, "end": v(-195.7, -60) * mm});
            skLineSegment(sketch, "E102.2.19", {"start": v(-186.3, -50.59) * mm, "end": v(-177.2, -41.5) * mm});
            skLineSegment(sketch, "E102.2.20", {"start": v(-176.83, -67) * mm, "end": v(-176.83, -60) * mm});
            skLineSegment(sketch, "E102.2.21", {"start": v(-170.83, -54) * mm, "end": v(-184.88, -54) * mm});
            skLineSegment(sketch, "E102.2.22", {"start": v(-183.33, -72.5) * mm, "end": v(-183.33, -67) * mm});
            skLineSegment(sketch, "E102.2.23", {"start": v(-210.83, -56) * mm, "end": v(-210.83, -68) * mm});
            skLineSegment(sketch, "E102.2.24", {"start": v(-191.83, -33) * mm, "end": v(-191.83, -47.05) * mm});
            skLineSegment(sketch, "E102.2.25", {"start": v(-210.83, -36) * mm, "end": v(-210.83, -45) * mm});
            skLineSegment(sketch, "E102.2.26", {"start": v(-193.83, -73) * mm, "end": v(-205.83, -73) * mm});
            skArc(sketch, "E102.2.27", {"start": v(-203.33, -29.96) * mm, "mid": v(-199.7, -32.9) * mm, "end": v(-195.23, -31.57) * mm});
            skLineSegment(sketch, "E102.2.28", {"start": v(-204.83, -62) * mm, "end": v(-204.83, -55.5) * mm});
            skLineSegment(sketch, "E102.2.29", {"start": v(-204.83, -55.5) * mm, "end": v(-210.33, -55.5) * mm});
            skLineSegment(sketch, "E102.2.30", {"start": v(-183.33, -67) * mm, "end": v(-176.83, -67) * mm});
            skArc(sketch, "E102.2.31", {"start": v(-173.33, -28) * mm, "mid": v(-172.76, -30.87) * mm, "end": v(-171.13, -33.3) * mm});
            skLineSegment(sketch, "E102.2.32", {"start": v(-173.33, -28) * mm, "end": v(-165.83, -28) * mm, "construction": true});
            skLineSegment(sketch, "E102.2.33", {"start": v(-182.83, -72.5) * mm, "end": v(-183.33, -72.5) * mm});
            skArc(sketch, "E102.2.34", {"start": v(-195.23, -31.57) * mm, "mid": v(-193.06, -31.16) * mm, "end": v(-191.83, -33) * mm});
            skArc(sketch, "E102.2.35", {"start": v(-205.83, -73) * mm, "mid": v(-207.74, -72.62) * mm, "end": v(-209.37, -71.54) * mm});
            skLineSegment(sketch, "E102.2.36", {"start": v(-204.33, -29.96) * mm, "end": v(-203.33, -29.96) * mm});
            skArc(sketch, "E102.2.37", {"start": v(-191.83, -47.05) * mm, "mid": v(-190.6, -48.9) * mm, "end": v(-188.42, -48.46) * mm});
            skLineSegment(sketch, "E102.2.38", {"start": v(-201.95, -62) * mm, "end": v(-204.83, -62) * mm});
            skLineSegment(sketch, "E102.2.39", {"start": v(-210.33, -45) * mm, "end": v(-210.33, -45.5) * mm});
            skLineSegment(sketch, "E102.2.40", {"start": v(-199.83, -64.12) * mm, "end": v(-199.83, -67) * mm});
            skLineSegment(sketch, "E102.2.41", {"start": v(-204.33, -28) * mm, "end": v(-204.33, -29.96) * mm});
            skArc(sketch, "E102.2.42", {"start": v(-169.4, -57.4) * mm, "mid": v(-168.99, -55.23) * mm, "end": v(-170.83, -54) * mm});
            skArc(sketch, "E102.2.43", {"start": v(-210.83, -68) * mm, "mid": v(-210.45, -69.91) * mm, "end": v(-209.37, -71.54) * mm});
            skLineSegment(sketch, "E102.2.44", {"start": v(-167.79, -66.5) * mm, "end": v(-167.79, -65.5) * mm});
            skLineSegment(sketch, "E102.2.45", {"start": v(-210.83, -45) * mm, "end": v(-210.33, -45) * mm});
            skLineSegment(sketch, "E102.2.46", {"start": v(-210.33, -36) * mm, "end": v(-210.83, -36) * mm});
            skLineSegment(sketch, "E102.2.47", {"start": v(-165.83, -66.5) * mm, "end": v(-167.79, -66.5) * mm});
            skArc(sketch, "E102.2.48", {"start": v(-184.88, -54) * mm, "mid": v(-186.73, -52.77) * mm, "end": v(-186.3, -50.59) * mm});
            skLineSegment(sketch, "E102.2.49", {"start": v(-182.83, -73) * mm, "end": v(-182.83, -72.5) * mm});
            skLineSegment(sketch, "E102.2.50", {"start": v(-173.83, -72.5) * mm, "end": v(-173.83, -73) * mm});
            skLineSegment(sketch, "E102.2.51", {"start": v(-193.33, -72.5) * mm, "end": v(-193.83, -72.5) * mm});
            skLineSegment(sketch, "E102.2.52", {"start": v(-193.83, -72.5) * mm, "end": v(-193.83, -73) * mm});
            skLineSegment(sketch, "E102.2.53", {"start": v(-210.33, -55.5) * mm, "end": v(-210.33, -56) * mm});
            skLineSegment(sketch, "E102.2.54", {"start": v(-210.33, -56) * mm, "end": v(-210.83, -56) * mm});
            skArc(sketch, "E102.3.0", {"start": v(-173.33, -28) * mm, "mid": v(-172.76, -25.13) * mm, "end": v(-171.13, -22.7) * mm});
            skLineSegment(sketch, "E102.3.1", {"start": v(-197.83, 1.88) * mm, "end": v(-201.95, 6) * mm});
            skArc(sketch, "E102.3.2", {"start": v(-203.33, -26.04) * mm, "mid": v(-199.7, -23.1) * mm, "end": v(-195.23, -24.43) * mm});
            skLineSegment(sketch, "E102.3.3", {"start": v(-165.83, 16.5) * mm, "end": v(-173.83, 16.5) * mm});
            skLineSegment(sketch, "E102.3.4", {"start": v(-210.83, -20) * mm, "end": v(-210.83, -11) * mm});
            skLineSegment(sketch, "E102.3.5", {"start": v(-210.33, -28) * mm, "end": v(-210.33, -20) * mm});
            skLineSegment(sketch, "E102.3.6", {"start": v(-183.33, 16.5) * mm, "end": v(-183.33, 11) * mm});
            skLineSegment(sketch, "E102.3.7", {"start": v(-173.33, -28) * mm, "end": v(-165.83, -28) * mm, "construction": true});
            skLineSegment(sketch, "E102.3.8", {"start": v(-177.2, -14.5) * mm, "end": v(-165.83, -14.5) * mm});
            skLineSegment(sketch, "E102.3.9", {"start": v(-176.83, 11) * mm, "end": v(-176.83, 4) * mm});
            skLineSegment(sketch, "E102.3.10", {"start": v(-204.83, -0.5) * mm, "end": v(-210.33, -0.5) * mm});
            skLineSegment(sketch, "E102.3.11", {"start": v(-183.33, 11) * mm, "end": v(-176.83, 11) * mm});
            skLineSegment(sketch, "E102.3.12", {"start": v(-176.83, 4) * mm, "end": v(-195.7, 4) * mm});
            skLineSegment(sketch, "E102.3.13", {"start": v(-171.13, -22.7) * mm, "end": v(-165.83, -28) * mm, "construction": true});
            skLineSegment(sketch, "E102.3.14", {"start": v(-186.3, -5.41) * mm, "end": v(-177.2, -14.5) * mm});
            skLineSegment(sketch, "E102.3.15", {"start": v(-204.83, 6) * mm, "end": v(-204.83, -0.5) * mm});
            skLineSegment(sketch, "E102.3.16", {"start": v(-179.33, -16.62) * mm, "end": v(-179.33, -28) * mm});
            skLineSegment(sketch, "E102.3.17", {"start": v(-195.7, 4) * mm, "end": v(-199.83, 8.12) * mm});
            skLineSegment(sketch, "E102.3.18", {"start": v(-197.83, -17) * mm, "end": v(-197.83, 1.88) * mm});
            skLineSegment(sketch, "E102.3.19", {"start": v(-188.42, -7.54) * mm, "end": v(-179.33, -16.62) * mm});
            skLineSegment(sketch, "E102.3.20", {"start": v(-204.83, -17) * mm, "end": v(-197.83, -17) * mm});
            skLineSegment(sketch, "E102.3.21", {"start": v(-191.83, -23) * mm, "end": v(-191.83, -8.95) * mm});
            skLineSegment(sketch, "E102.3.22", {"start": v(-210.33, -10.5) * mm, "end": v(-204.83, -10.5) * mm});
            skLineSegment(sketch, "E102.3.23", {"start": v(-193.83, 17) * mm, "end": v(-205.83, 17) * mm});
            skLineSegment(sketch, "E102.3.24", {"start": v(-170.83, -2) * mm, "end": v(-184.88, -2) * mm});
            skLineSegment(sketch, "E102.3.25", {"start": v(-173.83, 17) * mm, "end": v(-182.83, 17) * mm});
            skLineSegment(sketch, "E102.3.26", {"start": v(-210.83, 0) * mm, "end": v(-210.83, 12) * mm});
            skArc(sketch, "E102.3.27", {"start": v(-167.79, 9.5) * mm, "mid": v(-170.73, 5.88) * mm, "end": v(-169.4, 1.4) * mm});
            skLineSegment(sketch, "E102.3.28", {"start": v(-199.83, 11) * mm, "end": v(-193.33, 11) * mm});
            skLineSegment(sketch, "E102.3.29", {"start": v(-193.33, 11) * mm, "end": v(-193.33, 16.5) * mm});
            skLineSegment(sketch, "E102.3.30", {"start": v(-204.83, -10.5) * mm, "end": v(-204.83, -17) * mm});
            skArc(sketch, "E102.3.31", {"start": v(-165.83, -20.5) * mm, "mid": v(-168.7, -21.07) * mm, "end": v(-171.13, -22.7) * mm});
            skLineSegment(sketch, "E102.3.33", {"start": v(-210.33, -11) * mm, "end": v(-210.33, -10.5) * mm});
            skArc(sketch, "E102.3.34", {"start": v(-169.4, 1.4) * mm, "mid": v(-168.99, -0.77) * mm, "end": v(-170.83, -2) * mm});
            skArc(sketch, "E102.3.35", {"start": v(-210.83, 12) * mm, "mid": v(-210.45, 13.91) * mm, "end": v(-209.37, 15.54) * mm});
            skLineSegment(sketch, "E102.3.36", {"start": v(-167.79, 10.5) * mm, "end": v(-167.79, 9.5) * mm});
            skArc(sketch, "E102.3.37", {"start": v(-184.88, -2) * mm, "mid": v(-186.73, -3.23) * mm, "end": v(-186.3, -5.41) * mm});
            skLineSegment(sketch, "E102.3.38", {"start": v(-199.83, 8.12) * mm, "end": v(-199.83, 11) * mm});
            skLineSegment(sketch, "E102.3.39", {"start": v(-182.83, 16.5) * mm, "end": v(-183.33, 16.5) * mm});
            skLineSegment(sketch, "E102.3.40", {"start": v(-201.95, 6) * mm, "end": v(-204.83, 6) * mm});
            skLineSegment(sketch, "E102.3.41", {"start": v(-165.83, 10.5) * mm, "end": v(-167.79, 10.5) * mm});
            skArc(sketch, "E102.3.42", {"start": v(-195.23, -24.43) * mm, "mid": v(-193.06, -24.84) * mm, "end": v(-191.83, -23) * mm});
            skArc(sketch, "E102.3.43", {"start": v(-205.83, 17) * mm, "mid": v(-207.74, 16.62) * mm, "end": v(-209.37, 15.54) * mm});
            skLineSegment(sketch, "E102.3.44", {"start": v(-204.33, -26.04) * mm, "end": v(-203.33, -26.04) * mm});
            skLineSegment(sketch, "E102.3.45", {"start": v(-182.83, 17) * mm, "end": v(-182.83, 16.5) * mm});
            skLineSegment(sketch, "E102.3.46", {"start": v(-173.83, 16.5) * mm, "end": v(-173.83, 17) * mm});
            skLineSegment(sketch, "E102.3.47", {"start": v(-204.33, -28) * mm, "end": v(-204.33, -26.04) * mm});
            skArc(sketch, "E102.3.48", {"start": v(-191.83, -8.95) * mm, "mid": v(-190.6, -7.1) * mm, "end": v(-188.42, -7.54) * mm});
            skLineSegment(sketch, "E102.3.49", {"start": v(-210.83, -11) * mm, "end": v(-210.33, -11) * mm});
            skLineSegment(sketch, "E102.3.50", {"start": v(-210.33, -20) * mm, "end": v(-210.83, -20) * mm});
            skLineSegment(sketch, "E102.3.51", {"start": v(-210.33, -0.5) * mm, "end": v(-210.33, 0) * mm});
            skLineSegment(sketch, "E102.3.52", {"start": v(-210.33, 0) * mm, "end": v(-210.83, 0) * mm});
            skLineSegment(sketch, "E102.3.53", {"start": v(-193.33, 16.5) * mm, "end": v(-193.83, 16.5) * mm});
            skLineSegment(sketch, "E102.3.54", {"start": v(-193.83, 16.5) * mm, "end": v(-193.83, 17) * mm});
            skPoint(sketch, "E102.center", {"position": v(-165.83, -28) * mm});
            skLineSegment(sketch, "E102.anchor1", {"start": v(-165.83, -28) * mm, "end": v(-165.83, 16.5) * mm, "construction": true});
            skLineSegment(sketch, "E102.anchor2", {"start": v(-165.83, -28) * mm, "end": v(-210.33, -28) * mm, "construction": true});
            skSolve(sketch);
        }
        {
            var Q0;
            Q0=makeQuery(id+"F0.imprint","IMPRINT",FACE,{"disambiguationData":[TD([[makeQuery(id+"F0.imprint","IMPRINT",EDGE,{"derivedFrom":sQuery(id+"F0.wireOp",EDGE,"E46.1.0")}),1.0]])]});
            var Q1;
            Q1=makeQuery(id+"F0.imprint","IMPRINT",FACE,{"disambiguationData":[TD([[makeQuery(id+"F0.imprint","IMPRINT",EDGE,{"derivedFrom":sQuery(id+"F0.wireOp",EDGE,"E0")}),1.0]])]});
            var Q2;
            Q2=makeQuery(id+"F0.imprint","IMPRINT",FACE,{"disambiguationData":[TD([[makeQuery(id+"F0.imprint","IMPRINT",EDGE,{"derivedFrom":sQuery(id+"F0.wireOp",EDGE,"E46.2.0")}),1.0]])]});
            var Q3;
            Q3=makeQuery(id+"F0.imprint","IMPRINT",FACE,{"disambiguationData":[TD([[makeQuery(id+"F0.imprint","IMPRINT",EDGE,{"derivedFrom":sQuery(id+"F0.wireOp",EDGE,"E46.3.0")}),1.0]])]});
            extrude(context, id + "F1", {"entities" : qUnion([Q0, Q1, Q2, Q3]), "depth" : 1000 * mm});
        }
        {
            var Q0;
            Q0=makeQuery(id+"F0.imprint","IMPRINT",FACE,{"disambiguationData":[TD([[makeQuery(id+"F0.imprint","IMPRINT",EDGE,{"derivedFrom":sQuery(id+"F0.wireOp",EDGE,"E47")}),-1.0]])]});
            extrude(context, id + "F2", {"entities" : qUnion([Q0]), "depth" : 1000 * mm});
        }
    });
